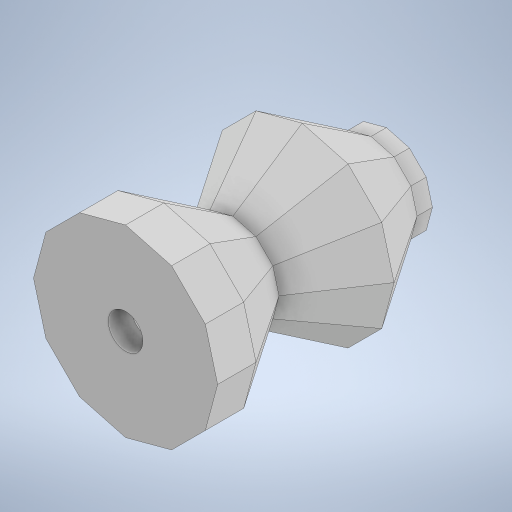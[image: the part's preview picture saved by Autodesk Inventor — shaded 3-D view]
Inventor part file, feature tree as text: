
AUTODESK INVENTOR PART (.ipt)
format: ipt  version: 2023 (Build 270158000, 158)  size: 354,816 bytes
history: native  units: in
note: dims shown in document units (in); Inventor stores cm internally (conversion verified against a paired STEP export)
features: sketch x6, extrude x4, projected_geometry x3, other x2, mirror x2, loft x1, shell x1
ambient origin geometry x8: Origin, YZ Plane, XZ Plane, XY Plane, X Axis, Y Axis, Z Axis, Center Point
bodies: Body1 (feature_tree)
feature tree (19):
  other  "솔리드1"
  sketch  "스케치1"
  other  "작업 평면1"
  loft  "로프트1"
  mirror  "미러1"
  mirror  "미러2"
  extrude  "돌출1"  Depth=0.3543in
  shell  "쉘3"  Thickness=0.4724in
  extrude  "돌출8"  TaperAngle=0.0deg  [1 undecoded]
  extrude  "돌출9"  TaperAngle=0.0deg  [1 undecoded]
  extrude  "돌출10"  Depth=0.1142in TaperAngle=0.0deg
  sketch  "스케치2"
  sketch  "스케치3"
  projected_geometry  "투영된 루프1"
  sketch  "스케치10"
  projected_geometry  "투영된 루프6"
  sketch  "스케치11"
  sketch  "스케치12"
  projected_geometry  "투영된 루프7"
note: 2 required parameter values undecoded (feature->parameter linkage not recoverable at this tier; creation-order binding heuristic only, values carry confidence <= 0.55)
